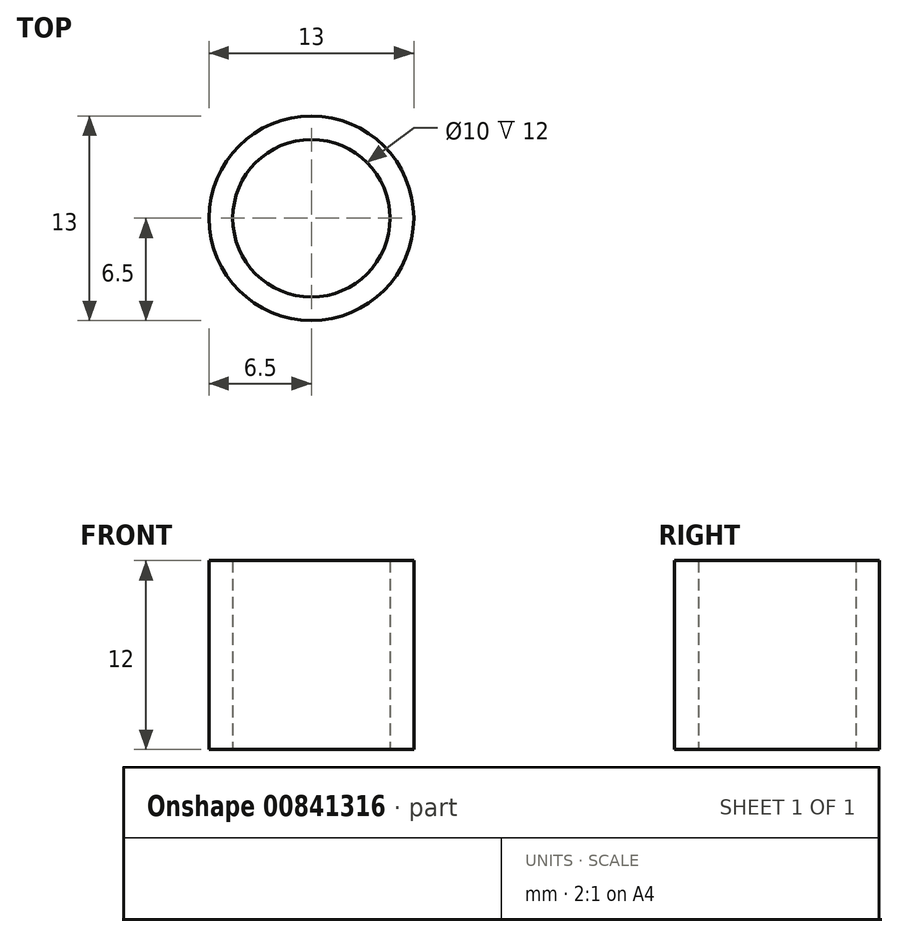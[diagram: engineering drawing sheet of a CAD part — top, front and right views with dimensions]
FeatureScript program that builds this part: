
annotation { "Feature Type Name" : "Feature", "Feature Type Description" : "" }
export const myFeature = defineFeature(function(context is Context, id is Id, definition is map)
    precondition{}
    {
        {
            var Q0;
            Q0=qCreatedBy(makeId("Top.planeOp"),FACE);
            var sketch = newSketch(context, id + "F0", { "sketchPlane" : qUnion([Q0])});
            skCircle(sketch, "E0", {"center": v(0, 0) * mm, "radius": 6.5 * mm});
            skCircle(sketch, "E1", {"center": v(0, 0) * mm, "radius": 5 * mm});
            skSolve(sketch);
        }
        {
            var Q0;
            Q0 = qSketchRegion(id + "F0", true);
            extrude(context, id + "F1", {"entities" : qUnion([Q0]), "depth" : 12 * mm, "offsetDistance" : 25.4 * mm});
        }
    });
